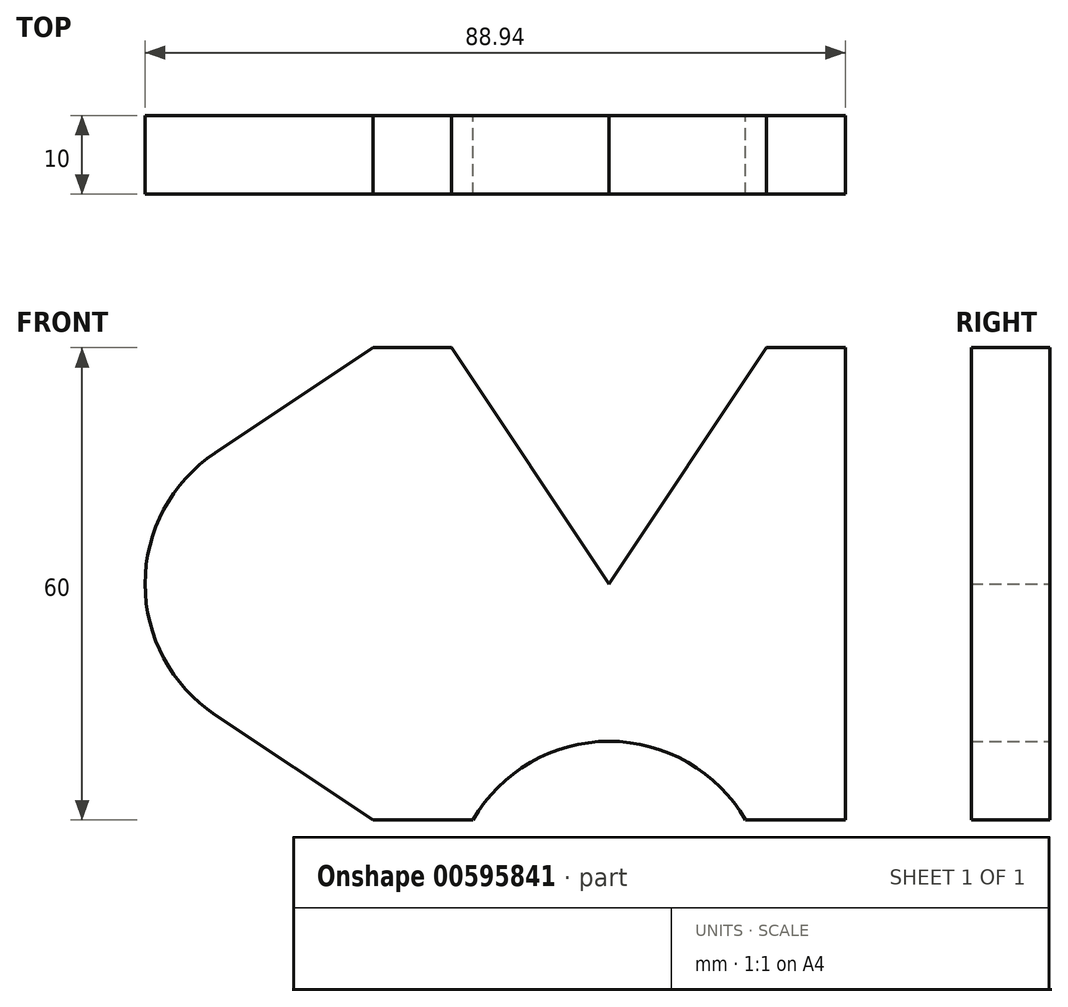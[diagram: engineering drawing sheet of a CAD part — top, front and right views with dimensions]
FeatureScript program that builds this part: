
annotation { "Feature Type Name" : "Feature", "Feature Type Description" : "" }
export const myFeature = defineFeature(function(context is Context, id is Id, definition is map)
    precondition{}
    {
        {
            var Q0;
            Q0=qCreatedBy(makeId("Front.planeOp"),FACE);
            var sketch = newSketch(context, id + "F0", { "sketchPlane" : qUnion([Q0])});
            skLineSegment(sketch, "E0", {"start": v(-20, 30) * mm, "end": v(0, 0) * mm});
            skLineSegment(sketch, "E1", {"start": v(0, 0) * mm, "end": v(20, 30) * mm});
            skLineSegment(sketch, "E2", {"start": v(20, 30) * mm, "end": v(30, 30) * mm});
            skLineSegment(sketch, "E3", {"start": v(30, 30) * mm, "end": v(30, -30) * mm});
            skLineSegment(sketch, "E4", {"start": v(30, -30) * mm, "end": v(17.32, -30) * mm});
            skArc(sketch, "E5", {"start": v(17.32, -30) * mm, "mid": v(0, -20) * mm, "end": v(-17.32, -30) * mm});
            skLineSegment(sketch, "E6", {"start": v(-17.32, -30) * mm, "end": v(-30, -30) * mm});
            skLineSegment(sketch, "E7", {"start": v(-30, -30) * mm, "end": v(-50.04, -16.64) * mm});
            skLineSegment(sketch, "E8", {"start": v(-20, 30) * mm, "end": v(-30, 30) * mm});
            skLineSegment(sketch, "E9", {"start": v(-30, 30) * mm, "end": v(-50.04, 16.64) * mm});
            skArc(sketch, "E10", {"start": v(-50.04, 16.64) * mm, "mid": v(-58.94, 0) * mm, "end": v(-50.04, -16.64) * mm});
            skLineSegment(sketch, "E11", {"start": v(-30, 30) * mm, "end": v(-30, -30) * mm, "construction": true});
            skSolve(sketch);
        }
        {
            var Q0;
            Q0=makeQuery(id+"F0.imprint","IMPRINT",FACE,{"disambiguationData":[TD([[makeQuery(id+"F0.imprint","IMPRINT",EDGE,{"derivedFrom":sQuery(id+"F0.wireOp",EDGE,"E0")}),-1.0]])]});
            extrude(context, id + "F1", {"entities" : qUnion([Q0]), "depth" : 10 * mm, "offsetDistance" : 25 * mm});
        }
    });
